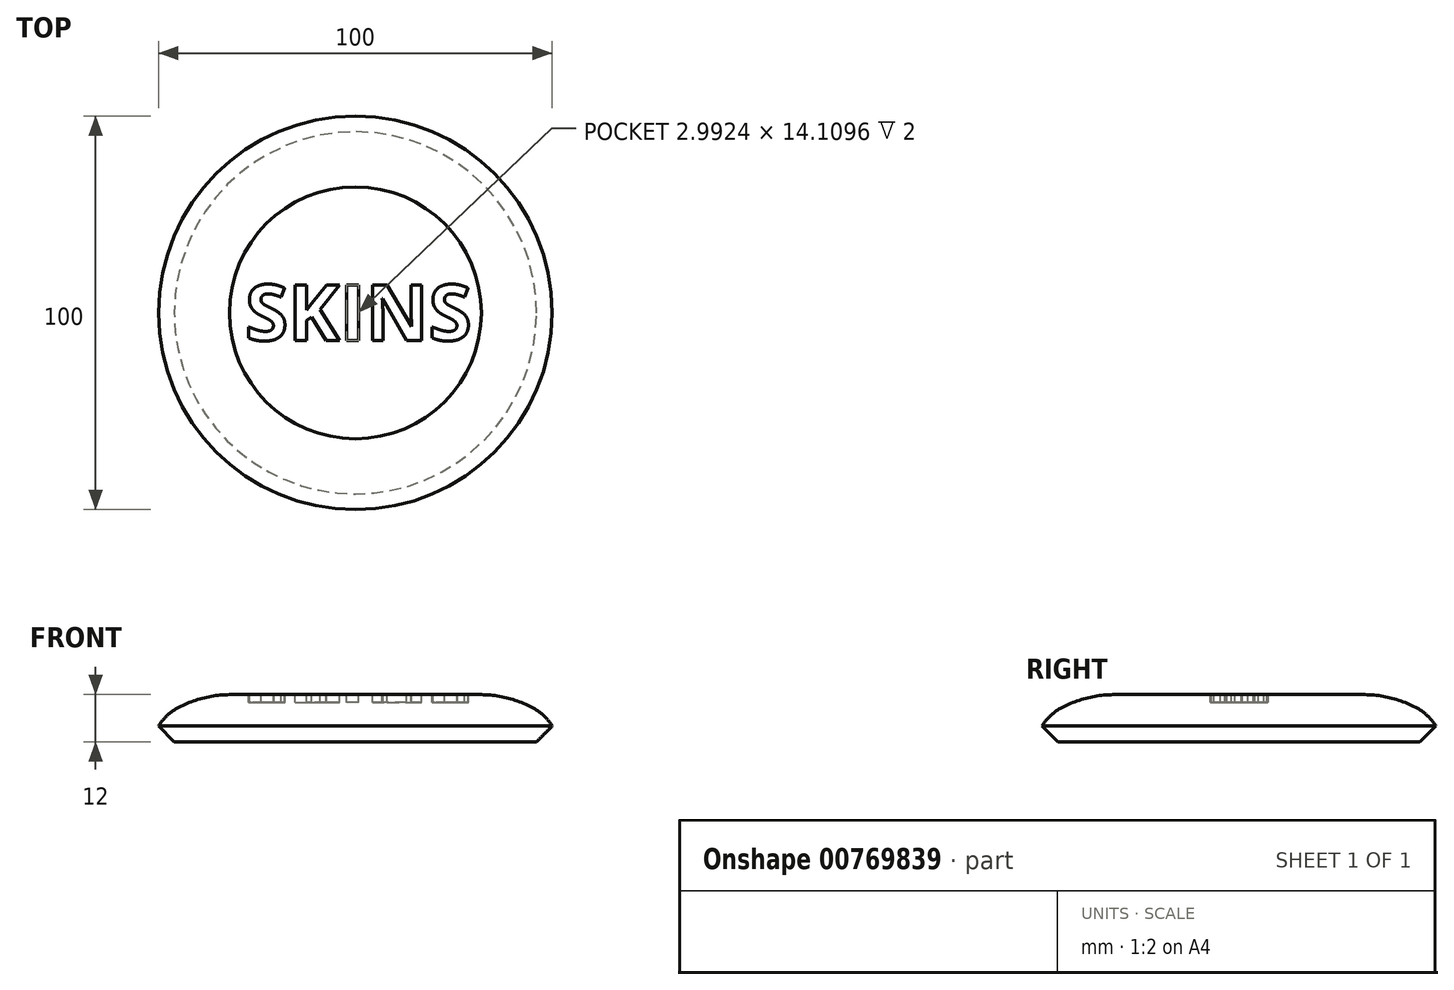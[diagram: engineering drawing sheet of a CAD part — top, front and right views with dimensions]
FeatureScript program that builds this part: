
annotation { "Feature Type Name" : "Feature", "Feature Type Description" : "" }
export const myFeature = defineFeature(function(context is Context, id is Id, definition is map)
    precondition{}
    {
        {
            var Q0;
            Q0=qCreatedBy(makeId("Top.planeOp"),FACE);
            var sketch = newSketch(context, id + "F0", { "sketchPlane" : qUnion([Q0])});
            skCircle(sketch, "E0", {"center": v(0, 0) * mm, "radius": 50 * mm});
            skSolve(sketch);
        }
        {
            var Q0;
            Q0=qSketchRegion(id+"F0",true);
            extrude(context, id + "F1", {"entities" : qUnion([Q0]), "depth" : 12 * mm, "offsetDistance" : 25 * mm});
        }
        {
            var Q0;
            Q0=makeQuery(id+"F1.opExtrude","CAP_FACE",FACE,{"disambiguationData":[OSD([sQuery(id+"F0.wireOp",EDGE,"E0")])],"isStart":true});
            chamfer(context, id + "F2", {"entities" : qUnion([Q0]), "width" : 4 * mm, "tangentPropagation" : true});
        }
        {
            var Q0;
            Q0=qCreatedBy(makeId("Front.planeOp"),FACE);
            var sketch = newSketch(context, id + "F3", { "sketchPlane" : qUnion([Q0])});
            skLineSegment(sketch, "E1", {"start": v(-32, 12) * mm, "end": v(-32, 25.16) * mm});
            skLineSegment(sketch, "E2", {"start": v(-41, 13.4) * mm, "end": v(-41, 24.79) * mm});
            skLineSegment(sketch, "E3", {"start": v(-50, 4) * mm, "end": v(-50, 25.02) * mm});
            skArc(sketch, "E4", {"start": v(-44.87, 8.8) * mm, "mid": v(-47.77, 6.75) * mm, "end": v(-50, 4) * mm});
            skArc(sketch, "E5", {"start": v(-32, 12) * mm, "mid": v(-38.62, 11.15) * mm, "end": v(-44.87, 8.8) * mm});
            skLineSegment(sketch, "E6", {"start": v(-54.4, 12) * mm, "end": v(-50, 12) * mm});
            skLineSegment(sketch, "E7", {"start": v(-50, 4) * mm, "end": v(-50, 12) * mm});
            skLineSegment(sketch, "E8", {"start": v(0, 10.8) * mm, "end": v(0, 54.2) * mm});
            skLineSegment(sketch, "E9", {"start": v(-50, 12) * mm, "end": v(-32, 12) * mm});
            skSolve(sketch);
        }
        {
            var Q0;
            Q0=qSketchRegion(id+"F3",true);
            var Q1;
            Q1=sQuery(id+"F3.wireOp",EDGE,"E8");
            revolve(context, id + "F4", {"operationType" : NewBodyOperationType.REMOVE, "surfaceOperationType" : NewSurfaceOperationType.NEW, "entities" : qUnion([Q0]), "axis" : qUnion([Q1]), "revolveType" : RevolveType.FULL, "oppositeDirection" : true});
        }
        {
            var Q0;
            Q0=makeQuery(id+"F1.opExtrude","CAP_FACE",FACE,{"disambiguationData":[OSD([sQuery(id+"F0.wireOp",EDGE,"E0")])],"isStart":false});
            var sketch = newSketch(context, id + "F5", { "sketchPlane" : qUnion([Q0])});
            skText(sketch, "E10", { "text": "SKINS", "fontName": "OpenSans-Bold.ttf"});
            const initialGuessF5  = {"E10": [-0.028, -0.007, 1, 0, 0.01423]};
            skSetInitialGuess(sketch, initialGuessF5);
            skSolve(sketch);
        }
        {
            var Q0;
            Q0=qSketchRegion(id+"F5",true);
            extrude(context, id + "F6", {"entities" : qUnion([Q0]), "operationType" : NewBodyOperationType.REMOVE, "oppositeDirection" : true, "depth" : 2 * mm, "offsetDistance" : 25 * mm});
        }
    });
